# Revit family: Camera-Security-HanwhaTechwin-Bullet-Wisenet X-XNO-C6083R_inch_
name_source: partatom
category: Security Devices
revit_build: Autodesk Revit 2016 (Build: 20151007_0715(x64)
units: mm (PartAtom-declared; Revit-internal decimal feet)

## family parameters
Cut with Voids When Loaded = No
Host = Face
Maintain Annotation Orientation = Yes
OmniClass Number = 23.85.30.17.14
OmniClass Title = Video Surveillance
Part Type = Normal
Room Calculation Point = No
Round Connector Dimension = Use Diameter
Shared = No

## types (1)
- Standard
    Default Elevation = 48 "
    Description = NBS standard template for generic face-based components
    Manufacturer = Hanwha Techwin
    Model = XNO-C6083R
    Product Documentation Link = https://www.hanwha-security.com
    Product Material = Aluminum - HanwhaTechwin - White
    Product Page URL = https://www.hanwha-security.com
    URL = https://www.hanwha-security.com

## geometry (parser evidence)
native form markers: Sweep x10
no freeform markers — native parametric forms only
